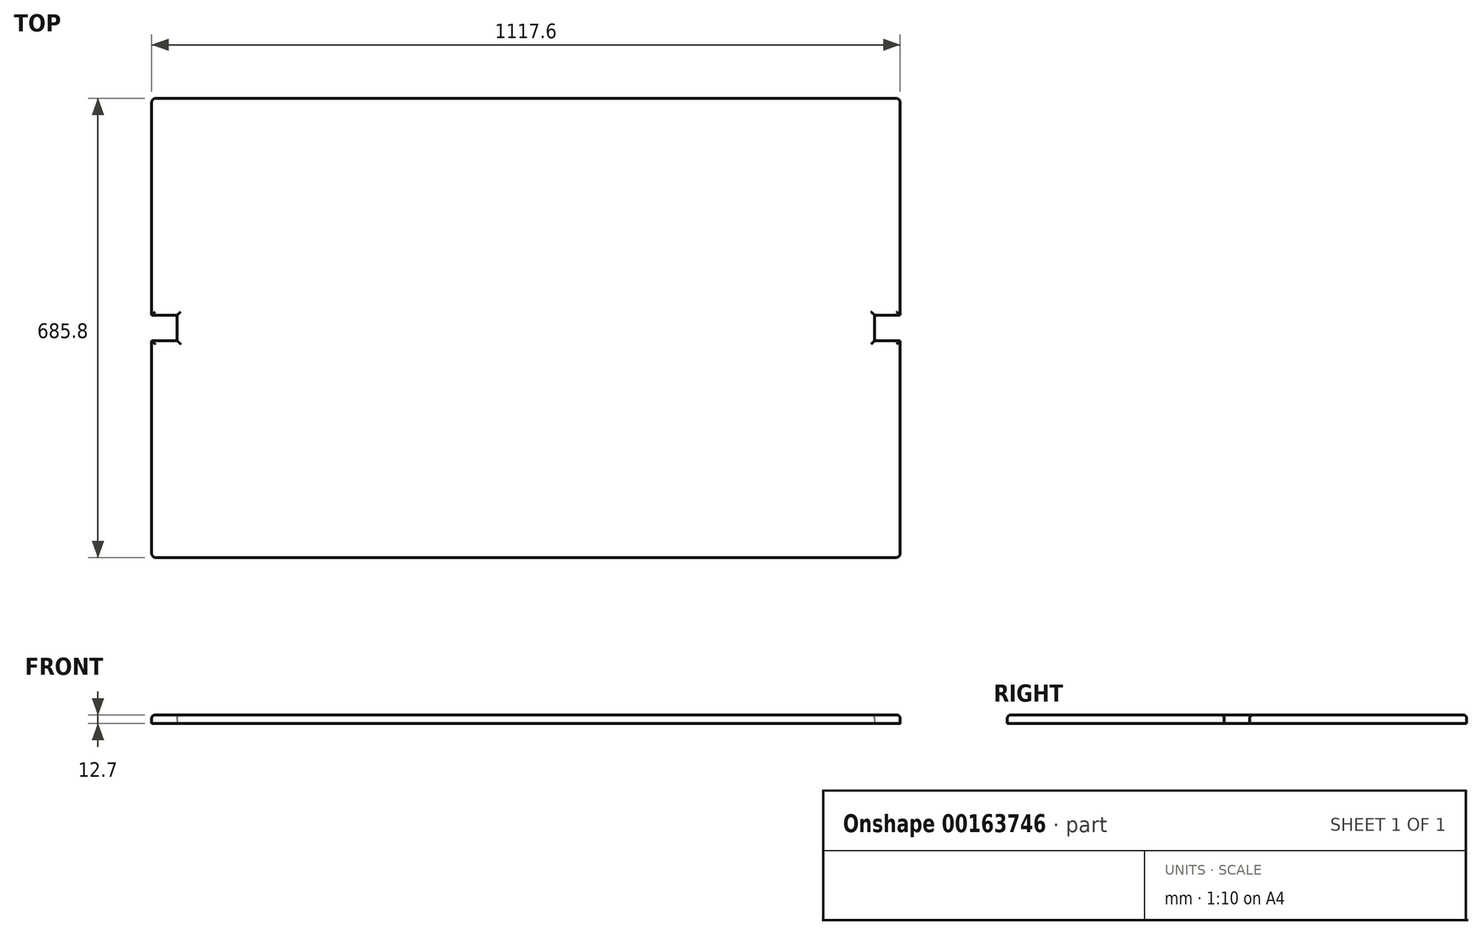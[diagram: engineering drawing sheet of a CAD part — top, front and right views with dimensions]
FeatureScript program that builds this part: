
annotation { "Feature Type Name" : "Feature", "Feature Type Description" : "" }
export const myFeature = defineFeature(function(context is Context, id is Id, definition is map)
    precondition{}
    {
        {
            var Q0;
            Q0=qCreatedBy(makeId("Top.planeOp"),FACE);
            var sketch = newSketch(context, id + "F0", { "sketchPlane" : qUnion([Q0])});
            skLineSegment(sketch, "E0.bottom", {"start": v(552.45, -342.9) * mm, "end": v(-552.45, -342.9) * mm});
            skLineSegment(sketch, "E0.top", {"start": v(552.45, 342.9) * mm, "end": v(-552.45, 342.9) * mm});
            skLineSegment(sketch, "E0.left", {"start": v(558.8, -336.55) * mm, "end": v(558.8, -19.05) * mm});
            skLineSegment(sketch, "E0.right", {"start": v(-558.8, -336.55) * mm, "end": v(-558.8, -19.05) * mm});
            skPoint(sketch, "E0.middle", {"position": v(0, 0) * mm});
            skPoint(sketch, "E1.visualSharp", {"position": v(-558.8, 342.9) * mm});
            skArc(sketch, "E1.filletArc", {"start": v(-552.45, 342.9) * mm, "mid": v(-556.94, 341.04) * mm, "end": v(-558.8, 336.55) * mm});
            skPoint(sketch, "E2.visualSharp", {"position": v(-558.8, -342.9) * mm});
            skArc(sketch, "E2.filletArc", {"start": v(-558.8, -336.55) * mm, "mid": v(-556.94, -341.04) * mm, "end": v(-552.45, -342.9) * mm});
            skPoint(sketch, "E3.visualSharp", {"position": v(558.8, -342.9) * mm});
            skArc(sketch, "E3.filletArc", {"start": v(552.45, -342.9) * mm, "mid": v(556.94, -341.04) * mm, "end": v(558.8, -336.55) * mm});
            skPoint(sketch, "E4.visualSharp", {"position": v(558.8, 342.9) * mm});
            skArc(sketch, "E4.filletArc", {"start": v(558.8, 336.55) * mm, "mid": v(556.94, 341.04) * mm, "end": v(552.45, 342.9) * mm});
            skLineSegment(sketch, "E5.bottom", {"start": v(-520.7, -19.05) * mm, "end": v(-558.8, -19.05) * mm});
            skLineSegment(sketch, "E5.top", {"start": v(-520.7, 19.05) * mm, "end": v(-558.8, 19.05) * mm});
            skLineSegment(sketch, "E5.left", {"start": v(-520.7, -19.05) * mm, "end": v(-520.7, 19.05) * mm});
            skLineSegment(sketch, "E6.trimOffspring", {"start": v(-558.8, 19.05) * mm, "end": v(-558.8, 336.55) * mm});
            skLineSegment(sketch, "E7", {"start": v(0, 0) * mm, "end": v(0, 342.9) * mm, "construction": true});
            skLineSegment(sketch, "E8.MirrorCS", {"start": v(520.7, 19.05) * mm, "end": v(558.8, 19.05) * mm});
            skLineSegment(sketch, "E9.MirrorCS", {"start": v(520.7, -19.05) * mm, "end": v(520.7, 19.05) * mm});
            skLineSegment(sketch, "E10.MirrorCS", {"start": v(520.7, -19.05) * mm, "end": v(558.8, -19.05) * mm});
            skLineSegment(sketch, "E11.trimOffspring", {"start": v(558.8, 19.05) * mm, "end": v(558.8, 336.55) * mm});
            skSolve(sketch);
        }
        {
            var Q0;
            Q0 = qSketchRegion(id + "F0", true);
            extrude(context, id + "F1", {"entities" : qUnion([Q0]), "depth" : 12.7 * mm});
        }
        {
            var Q0;
            Q0=makeQuery(id+"F1.opExtrude","CAP_FACE",FACE,{"disambiguationData":[OSD([sQuery(id+"F0.wireOp",EDGE,"E0.bottom"),sQuery(id+"F0.wireOp",EDGE,"E0.top"),sQuery(id+"F0.wireOp",EDGE,"E0.left"),sQuery(id+"F0.wireOp",EDGE,"E0.right"),sQuery(id+"F0.wireOp",EDGE,"E1.filletArc"),sQuery(id+"F0.wireOp",EDGE,"E2.filletArc"),sQuery(id+"F0.wireOp",EDGE,"E3.filletArc"),sQuery(id+"F0.wireOp",EDGE,"E4.filletArc")])],"isStart":false});
            fillet(context, id + "F2", {"entities" : qUnion([Q0]), "radius" : 5.08 * mm, "tangentPropagation" : true, "allowEdgeOverflow" : false});
        }
    });
